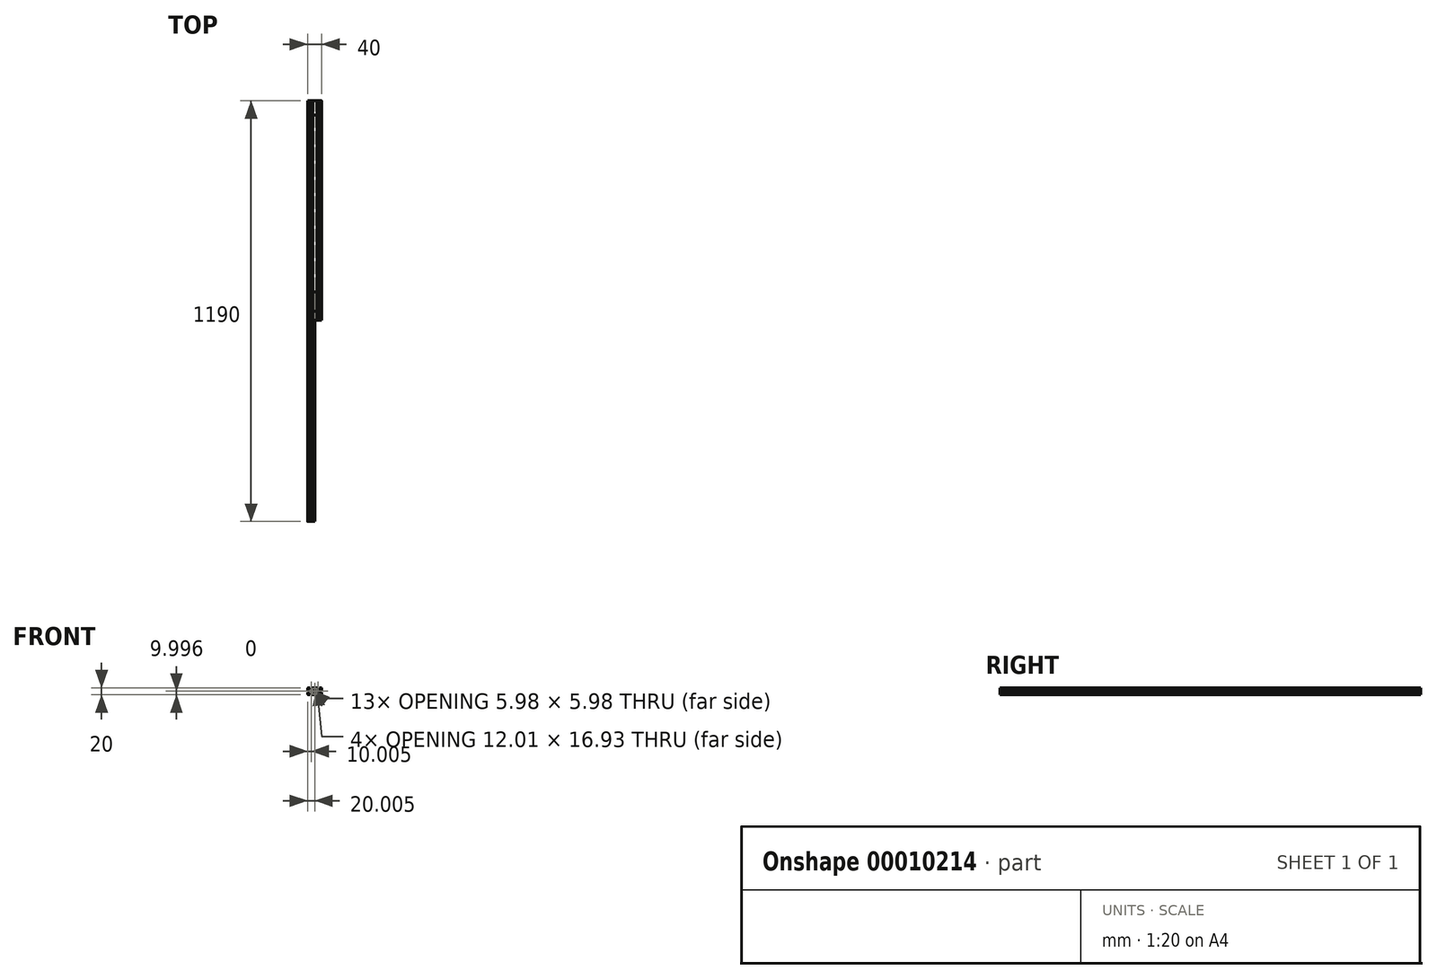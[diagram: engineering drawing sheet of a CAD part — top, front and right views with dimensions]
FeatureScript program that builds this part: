
annotation { "Feature Type Name" : "Feature", "Feature Type Description" : "" }
export const myFeature = defineFeature(function(context is Context, id is Id, definition is map)
    precondition{}
    {
        {
            var Q0;
            Q0=qCreatedBy(makeId("Front.planeOp"),FACE);
            var sketch = newSketch(context, id + "F0", { "sketchPlane" : qUnion([Q0])});
            skLineSegment(sketch, "E0.rect.bottom", {"start": v(-8.26, 10.09) * mm, "end": v(-3.52, 10.09) * mm});
            skLineSegment(sketch, "E0.rect.top", {"start": v(-8.26, -9.91) * mm, "end": v(-3.52, -9.91) * mm});
            skLineSegment(sketch, "E0.rect.left", {"start": v(-10, 8.34) * mm, "end": v(-10, 3.6) * mm});
            skLineSegment(sketch, "E0.rect.right", {"start": v(10, 8.34) * mm, "end": v(10, 3.6) * mm});
            skPoint(sketch, "E0.rect.middle", {"position": v(0, 0.09) * mm});
            skPoint(sketch, "E1.visualSharp", {"position": v(-10, 10.09) * mm});
            skArc(sketch, "E1.filletArc", {"start": v(-8.26, 10.09) * mm, "mid": v(-9.5, 9.57) * mm, "end": v(-10, 8.34) * mm});
            skPoint(sketch, "E2.visualSharp", {"position": v(10, 10.09) * mm});
            skArc(sketch, "E2.filletArc", {"start": v(10, 8.34) * mm, "mid": v(9.48, 9.57) * mm, "end": v(8.24, 10.09) * mm});
            skPoint(sketch, "E3.visualSharp", {"position": v(10, -9.91) * mm});
            skArc(sketch, "E3.filletArc", {"start": v(8.24, -9.91) * mm, "mid": v(9.48, -9.4) * mm, "end": v(10, -8.16) * mm});
            skPoint(sketch, "E4.visualSharp", {"position": v(-10, -9.91) * mm});
            skArc(sketch, "E4.filletArc", {"start": v(-10, -8.16) * mm, "mid": v(-9.5, -9.4) * mm, "end": v(-8.26, -9.91) * mm});
            skPoint(sketch, "E5.rect.middle", {"position": v(-10, 0.09) * mm});
            skPoint(sketch, "E6.rect.middle", {"position": v(0, -9.91) * mm});
            skPoint(sketch, "E7.4.MirrorP", {"position": v(0, 10.09) * mm});
            skPoint(sketch, "E8.4.MirrorP", {"position": v(10, 0.09) * mm});
            skLineSegment(sketch, "E9", {"start": v(-3, 9.47) * mm, "end": v(-3, 8.55) * mm});
            skLineSegment(sketch, "E10", {"start": v(-3, 8.55) * mm, "end": v(-6.2, 8.55) * mm});
            skLineSegment(sketch, "E11", {"start": v(-6.2, 8.55) * mm, "end": v(-6.2, 6.99) * mm});
            skLineSegment(sketch, "E12", {"start": v(-0.58, 4.59) * mm, "end": v(-3.8, 4.59) * mm});
            skLineSegment(sketch, "E13", {"start": v(-3.8, 4.59) * mm, "end": v(-6.2, 6.99) * mm});
            skLineSegment(sketch, "E14", {"start": v(-3.52, 10.09) * mm, "end": v(-3.52, 9.47) * mm});
            skLineSegment(sketch, "E15", {"start": v(-3.52, 9.47) * mm, "end": v(-3, 9.47) * mm});
            skLineSegment(sketch, "E16", {"start": v(0, 28.9) * mm, "end": v(0, 4.59) * mm});
            skLineSegment(sketch, "E17.0.MirrorCS", {"start": v(3.51, 10.09) * mm, "end": v(3.51, 9.47) * mm});
            skLineSegment(sketch, "E18.0.MirrorCS", {"start": v(3.51, 9.47) * mm, "end": v(3, 9.47) * mm});
            skLineSegment(sketch, "E19.0.MirrorCS", {"start": v(3, 8.55) * mm, "end": v(6.2, 8.55) * mm});
            skLineSegment(sketch, "E20.0.MirrorCS", {"start": v(6.2, 8.55) * mm, "end": v(6.2, 6.99) * mm});
            skLineSegment(sketch, "E21.0.MirrorCS", {"start": v(3.8, 4.59) * mm, "end": v(6.2, 6.99) * mm});
            skLineSegment(sketch, "E22.0.MirrorCS", {"start": v(3.51, -9.91) * mm, "end": v(3.51, -9.3) * mm});
            skLineSegment(sketch, "E23.0.MirrorCS", {"start": v(3.51, -9.3) * mm, "end": v(3, -9.3) * mm});
            skLineSegment(sketch, "E24.0.MirrorCS", {"start": v(3, -8.38) * mm, "end": v(6.2, -8.38) * mm});
            skLineSegment(sketch, "E25.0.MirrorCS", {"start": v(6.2, -8.38) * mm, "end": v(6.2, -6.81) * mm});
            skLineSegment(sketch, "E26.0.MirrorCS", {"start": v(3.8, -4.41) * mm, "end": v(6.2, -6.81) * mm});
            skLineSegment(sketch, "E27.0.MirrorCS", {"start": v(-0.58, -4.41) * mm, "end": v(-3.8, -4.41) * mm});
            skLineSegment(sketch, "E28.0.MirrorCS", {"start": v(-3.8, -4.41) * mm, "end": v(-6.2, -6.81) * mm});
            skLineSegment(sketch, "E29.0.MirrorCS", {"start": v(-6.2, -8.38) * mm, "end": v(-6.2, -6.81) * mm});
            skLineSegment(sketch, "E30.0.MirrorCS", {"start": v(-3, -8.38) * mm, "end": v(-6.2, -8.38) * mm});
            skLineSegment(sketch, "E31.0.MirrorCS", {"start": v(-3.52, -9.3) * mm, "end": v(-3, -9.3) * mm});
            skLineSegment(sketch, "E32.0.MirrorCS", {"start": v(-3.52, -9.91) * mm, "end": v(-3.52, -9.3) * mm});
            skLineSegment(sketch, "E33.0.MirrorCS", {"start": v(10, 3.6) * mm, "end": v(9.38, 3.6) * mm});
            skLineSegment(sketch, "E34.0.MirrorCS", {"start": v(9.38, 3.6) * mm, "end": v(9.38, 3.09) * mm});
            skLineSegment(sketch, "E35.0.MirrorCS", {"start": v(8.46, 3.09) * mm, "end": v(8.46, 6.29) * mm});
            skLineSegment(sketch, "E36.0.MirrorCS", {"start": v(8.46, 6.29) * mm, "end": v(6.9, 6.29) * mm});
            skLineSegment(sketch, "E37.0.MirrorCS", {"start": v(4.5, 3.89) * mm, "end": v(6.9, 6.29) * mm});
            skLineSegment(sketch, "E38.0.MirrorCS", {"start": v(4.5, 0.56) * mm, "end": v(4.5, 3.89) * mm});
            skLineSegment(sketch, "E39.0.MirrorCS", {"start": v(4.5, -3.71) * mm, "end": v(6.9, -6.11) * mm});
            skLineSegment(sketch, "E40.0.MirrorCS", {"start": v(8.46, -6.11) * mm, "end": v(6.9, -6.11) * mm});
            skLineSegment(sketch, "E41.0.MirrorCS", {"start": v(8.46, -2.91) * mm, "end": v(8.46, -6.11) * mm});
            skLineSegment(sketch, "E42.0.MirrorCS", {"start": v(9.38, -3.43) * mm, "end": v(9.38, -2.91) * mm});
            skLineSegment(sketch, "E43.0.MirrorCS", {"start": v(10, -3.43) * mm, "end": v(9.38, -3.43) * mm});
            skLineSegment(sketch, "E44.0.MirrorCS", {"start": v(-4.5, -3.71) * mm, "end": v(-6.9, -6.11) * mm});
            skLineSegment(sketch, "E45.0.MirrorCS", {"start": v(-8.47, -6.11) * mm, "end": v(-6.9, -6.11) * mm});
            skLineSegment(sketch, "E46.0.MirrorCS", {"start": v(-8.47, -2.91) * mm, "end": v(-8.47, -6.11) * mm});
            skLineSegment(sketch, "E47.0.MirrorCS", {"start": v(-4.5, 3.89) * mm, "end": v(-6.9, 6.29) * mm});
            skLineSegment(sketch, "E48.0.MirrorCS", {"start": v(-8.47, 6.29) * mm, "end": v(-6.9, 6.29) * mm});
            skLineSegment(sketch, "E49.0.MirrorCS", {"start": v(-8.47, 3.09) * mm, "end": v(-8.47, 6.29) * mm});
            skLineSegment(sketch, "E50.0.MirrorCS", {"start": v(-9.39, 3.6) * mm, "end": v(-9.39, 3.09) * mm});
            skLineSegment(sketch, "E51.0.MirrorCS", {"start": v(-10, 3.6) * mm, "end": v(-9.39, 3.6) * mm});
            skLineSegment(sketch, "E52.0.MirrorCS", {"start": v(-9.39, -3.43) * mm, "end": v(-9.39, -2.91) * mm});
            skLineSegment(sketch, "E53.0.MirrorCS", {"start": v(-10, -3.43) * mm, "end": v(-9.39, -3.43) * mm});
            skPoint(sketch, "E54", {"position": v(3, 10.09) * mm});
            skPoint(sketch, "E55", {"position": v(-3, 9.47) * mm});
            skPoint(sketch, "E56", {"position": v(-3, 10.09) * mm});
            skPoint(sketch, "E57", {"position": v(3, 9.47) * mm});
            skPoint(sketch, "E58", {"position": v(3.51, 10.09) * mm});
            skPoint(sketch, "E59", {"position": v(-3, 8.55) * mm});
            skPoint(sketch, "E60", {"position": v(-6.2, 8.55) * mm});
            skPoint(sketch, "E61", {"position": v(-6.2, 6.99) * mm});
            skPoint(sketch, "E62", {"position": v(-3.8, 4.59) * mm});
            skPoint(sketch, "E63", {"position": v(3.8, 4.59) * mm});
            skPoint(sketch, "E64", {"position": v(6.2, 6.99) * mm});
            skPoint(sketch, "E65", {"position": v(6.2, 8.55) * mm});
            skPoint(sketch, "E66", {"position": v(3, 8.55) * mm});
            skLineSegment(sketch, "E67.trimOffspring", {"start": v(3, 9.47) * mm, "end": v(3, 8.55) * mm});
            skLineSegment(sketch, "E68.trimOffspring", {"start": v(3.51, 10.09) * mm, "end": v(8.24, 10.09) * mm});
            skPoint(sketch, "E69.orphan", {"position": v(-3, 15.59) * mm});
            skPoint(sketch, "E7.2.MirrorCS.end.orphan", {"position": v(3, 15.59) * mm});
            skPoint(sketch, "E70", {"position": v(-10, 3.6) * mm});
            skPoint(sketch, "E71", {"position": v(-10, 3.09) * mm});
            skPoint(sketch, "E72", {"position": v(-9.39, 3.6) * mm});
            skPoint(sketch, "E73", {"position": v(-9.39, 3.09) * mm});
            skPoint(sketch, "E74", {"position": v(-8.47, 3.09) * mm});
            skPoint(sketch, "E75", {"position": v(-8.47, 6.29) * mm});
            skPoint(sketch, "E76", {"position": v(-6.9, 6.29) * mm});
            skPoint(sketch, "E77", {"position": v(-4.5, 3.89) * mm});
            skPoint(sketch, "E78", {"position": v(-4.5, -3.71) * mm});
            skPoint(sketch, "E79", {"position": v(-6.9, -6.11) * mm});
            skPoint(sketch, "E80", {"position": v(-8.44, -6.12) * mm});
            skPoint(sketch, "E81", {"position": v(-8.47, -2.91) * mm});
            skPoint(sketch, "E82", {"position": v(-9.39, -2.91) * mm});
            skPoint(sketch, "E83", {"position": v(-9.39, -3.43) * mm});
            skPoint(sketch, "E84", {"position": v(-10, -3.43) * mm});
            skPoint(sketch, "E85", {"position": v(-10, -2.91) * mm});
            skPoint(sketch, "E86", {"position": v(-3.52, -9.91) * mm});
            skPoint(sketch, "E87", {"position": v(-3, -9.91) * mm});
            skPoint(sketch, "E88", {"position": v(-3, -9.3) * mm});
            skPoint(sketch, "E89", {"position": v(-3.52, -9.3) * mm});
            skPoint(sketch, "E90", {"position": v(-3, -8.38) * mm});
            skPoint(sketch, "E91", {"position": v(-6.2, -8.38) * mm});
            skPoint(sketch, "E92", {"position": v(-6.2, -6.81) * mm});
            skPoint(sketch, "E93", {"position": v(-3.8, -4.41) * mm});
            skPoint(sketch, "E94", {"position": v(3.8, -4.41) * mm});
            skPoint(sketch, "E95", {"position": v(6.2, -6.81) * mm});
            skPoint(sketch, "E96", {"position": v(6.2, -8.38) * mm});
            skPoint(sketch, "E97", {"position": v(3, -8.38) * mm});
            skPoint(sketch, "E98", {"position": v(3, -9.3) * mm});
            skPoint(sketch, "E99", {"position": v(3.51, -9.3) * mm});
            skPoint(sketch, "E100", {"position": v(3, -9.91) * mm});
            skPoint(sketch, "E101", {"position": v(3.51, -9.91) * mm});
            skPoint(sketch, "E102", {"position": v(10, -3.43) * mm});
            skPoint(sketch, "E103", {"position": v(10, -2.91) * mm});
            skPoint(sketch, "E104", {"position": v(9.38, -2.91) * mm});
            skPoint(sketch, "E105", {"position": v(9.38, -3.43) * mm});
            skPoint(sketch, "E106", {"position": v(8.46, -2.91) * mm});
            skPoint(sketch, "E107", {"position": v(8.46, -6.11) * mm});
            skPoint(sketch, "E108", {"position": v(6.9, -6.11) * mm});
            skPoint(sketch, "E109", {"position": v(4.5, -3.71) * mm});
            skPoint(sketch, "E110", {"position": v(4.5, 3.89) * mm});
            skPoint(sketch, "E111", {"position": v(6.9, 6.29) * mm});
            skPoint(sketch, "E112", {"position": v(8.46, 6.29) * mm});
            skPoint(sketch, "E113", {"position": v(8.46, 3.09) * mm});
            skPoint(sketch, "E114", {"position": v(9.38, 3.09) * mm});
            skPoint(sketch, "E115", {"position": v(9.38, 3.6) * mm});
            skPoint(sketch, "E116", {"position": v(10, 3.6) * mm});
            skPoint(sketch, "E117", {"position": v(10, 3.09) * mm});
            skLineSegment(sketch, "E118.trimOffspring", {"start": v(10, -3.43) * mm, "end": v(10, -8.16) * mm});
            skLineSegment(sketch, "E119.trimOffspring", {"start": v(9.38, 3.09) * mm, "end": v(8.46, 3.09) * mm});
            skPoint(sketch, "E8.1.MirrorCS.start.orphan", {"position": v(15.5, 3.09) * mm});
            skLineSegment(sketch, "E120.trimOffspring", {"start": v(9.38, -2.91) * mm, "end": v(8.46, -2.91) * mm});
            skPoint(sketch, "E8.2.MirrorCS.start.orphan", {"position": v(15.5, -2.91) * mm});
            skLineSegment(sketch, "E121.trimOffspring", {"start": v(3.51, -9.91) * mm, "end": v(8.24, -9.91) * mm});
            skLineSegment(sketch, "E122.trimOffspring", {"start": v(3, -9.3) * mm, "end": v(3, -8.38) * mm});
            skLineSegment(sketch, "E123.trimOffspring", {"start": v(-3, -9.3) * mm, "end": v(-3, -8.38) * mm});
            skPoint(sketch, "E124.orphan", {"position": v(3, -15.41) * mm});
            skPoint(sketch, "E6.rect.bottom.start.orphan", {"position": v(-3, -15.41) * mm});
            skLineSegment(sketch, "E125.trimOffspring", {"start": v(-10, -3.43) * mm, "end": v(-10, -8.16) * mm});
            skLineSegment(sketch, "E126.trimOffspring", {"start": v(-9.39, -2.91) * mm, "end": v(-8.47, -2.91) * mm});
            skLineSegment(sketch, "E127.trimOffspring", {"start": v(-9.39, 3.09) * mm, "end": v(-8.47, 3.09) * mm});
            skPoint(sketch, "E5.rect.left.end.orphan", {"position": v(-15.5, -2.91) * mm});
            skPoint(sketch, "E5.rect.left.start.orphan", {"position": v(-15.5, 3.09) * mm});
            skArc(sketch, "E128", {"start": v(1.01, 2.64) * mm, "mid": v(0, 2.84) * mm, "end": v(-1.02, 2.64) * mm});
            skLineSegment(sketch, "E129", {"start": v(-0.58, 4.59) * mm, "end": v(0, 4.02) * mm});
            skLineSegment(sketch, "E130", {"start": v(-4.5, 0.56) * mm, "end": v(-4, 0.09) * mm});
            skLineSegment(sketch, "E131.0.MirrorCS", {"start": v(0.57, 4.59) * mm, "end": v(0, 4.02) * mm});
            skLineSegment(sketch, "E132.0.MirrorCS", {"start": v(4.5, 0.56) * mm, "end": v(4, 0.09) * mm});
            skLineSegment(sketch, "E133.0.MirrorCS", {"start": v(-4.5, -0.4) * mm, "end": v(-4, 0.09) * mm});
            skLineSegment(sketch, "E134.0.MirrorCS", {"start": v(4.5, -0.4) * mm, "end": v(4, 0.09) * mm});
            skLineSegment(sketch, "E135.0.MirrorCS", {"start": v(0.57, -4.41) * mm, "end": v(0, -3.84) * mm});
            skLineSegment(sketch, "E136.0.MirrorCS", {"start": v(-0.58, -4.41) * mm, "end": v(0, -3.84) * mm});
            skPoint(sketch, "E137.orphan", {"position": v(0, -4.41) * mm});
            skLineSegment(sketch, "E138", {"start": v(8.24, -8.16) * mm, "end": v(-10.9, 10.99) * mm, "construction": true});
            skLineSegment(sketch, "E139", {"start": v(-5.8, -1.82) * mm, "end": v(1.97, 5.95) * mm, "construction": true});
            skLineSegment(sketch, "E140", {"start": v(-3, 1.54) * mm, "end": v(-2.56, 1.1) * mm});
            skLineSegment(sketch, "E141.0.MirrorCS", {"start": v(-1.46, 3.08) * mm, "end": v(-1.02, 2.64) * mm});
            skLineSegment(sketch, "E142.0.MirrorCS", {"start": v(1.45, 3.08) * mm, "end": v(1.01, 2.64) * mm});
            skLineSegment(sketch, "E143.0.MirrorCS", {"start": v(2.98, 1.54) * mm, "end": v(2.55, 1.1) * mm});
            skLineSegment(sketch, "E144.0.MirrorCS", {"start": v(2.98, -1.37) * mm, "end": v(2.55, -0.93) * mm});
            skLineSegment(sketch, "E145.0.MirrorCS", {"start": v(1.45, -2.9) * mm, "end": v(1.01, -2.47) * mm});
            skLineSegment(sketch, "E146.0.MirrorCS", {"start": v(-1.46, -2.9) * mm, "end": v(-1.02, -2.47) * mm});
            skLineSegment(sketch, "E147.0.MirrorCS", {"start": v(-3, -1.37) * mm, "end": v(-2.56, -0.93) * mm});
            skArc(sketch, "E148.trimOffspring", {"start": v(-1.02, -2.47) * mm, "mid": v(0, -2.66) * mm, "end": v(1.01, -2.47) * mm});
            skArc(sketch, "E149.trimOffspring", {"start": v(2.55, -0.93) * mm, "mid": v(2.74, 0.09) * mm, "end": v(2.55, 1.1) * mm});
            skArc(sketch, "E150.trimOffspring", {"start": v(-2.56, 1.1) * mm, "mid": v(-2.76, 0.09) * mm, "end": v(-2.56, -0.93) * mm});
            skLineSegment(sketch, "E151", {"start": v(-3, -1.37) * mm, "end": v(-1.46, -2.9) * mm});
            skLineSegment(sketch, "E152", {"start": v(1.45, 3.08) * mm, "end": v(2.98, 1.54) * mm});
            skLineSegment(sketch, "E153", {"start": v(-1.46, 3.08) * mm, "end": v(-3, 1.54) * mm});
            skLineSegment(sketch, "E154", {"start": v(2.98, -1.37) * mm, "end": v(1.45, -2.9) * mm});
            skLineSegment(sketch, "E155", {"start": v(-4.5, 3.89) * mm, "end": v(-4.5, 0.56) * mm});
            skLineSegment(sketch, "E156", {"start": v(-4.5, -0.4) * mm, "end": v(-4.5, -3.71) * mm});
            skLineSegment(sketch, "E157", {"start": v(4.5, -0.4) * mm, "end": v(4.5, -3.71) * mm});
            skLineSegment(sketch, "E158", {"start": v(0.57, 4.59) * mm, "end": v(3.8, 4.59) * mm});
            skLineSegment(sketch, "E159", {"start": v(0.57, -4.41) * mm, "end": v(3.8, -4.41) * mm});
            skSolve(sketch);
        }
        {
            var Q0;
            Q0=qCreatedBy(makeId("Front.planeOp"),FACE);
            var sketch = newSketch(context, id + "F1", { "sketchPlane" : qUnion([Q0])});
            skLineSegment(sketch, "E160.0.0", {"start": v(-3.52, 10.09) * mm, "end": v(-8.26, 10.09) * mm});
            skArc(sketch, "E160.0.1", {"start": v(-8.26, 10.09) * mm, "mid": v(-9.5, 9.57) * mm, "end": v(-10, 8.34) * mm});
            skLineSegment(sketch, "E160.0.2", {"start": v(-10, 8.34) * mm, "end": v(-10, 3.6) * mm});
            skLineSegment(sketch, "E160.0.3", {"start": v(-10, 3.6) * mm, "end": v(-9.39, 3.6) * mm});
            skLineSegment(sketch, "E160.0.4", {"start": v(-9.39, 3.6) * mm, "end": v(-9.39, 3.09) * mm});
            skLineSegment(sketch, "E160.0.5", {"start": v(-9.39, 3.09) * mm, "end": v(-8.47, 3.09) * mm});
            skLineSegment(sketch, "E160.0.6", {"start": v(-8.47, 3.09) * mm, "end": v(-8.47, 6.29) * mm});
            skLineSegment(sketch, "E160.0.7", {"start": v(-8.47, 6.29) * mm, "end": v(-6.9, 6.29) * mm});
            skLineSegment(sketch, "E160.0.8", {"start": v(-6.9, 6.29) * mm, "end": v(-4.5, 3.89) * mm});
            skLineSegment(sketch, "E160.0.9", {"start": v(-4.5, 3.89) * mm, "end": v(-4.5, 0.56) * mm});
            skLineSegment(sketch, "E160.0.10", {"start": v(-4.5, 0.56) * mm, "end": v(-4, 0.09) * mm});
            skLineSegment(sketch, "E160.0.11", {"start": v(-4, 0.09) * mm, "end": v(-4.5, -0.4) * mm});
            skLineSegment(sketch, "E160.0.12", {"start": v(-4.5, -0.4) * mm, "end": v(-4.5, -3.71) * mm});
            skLineSegment(sketch, "E160.0.13", {"start": v(-4.5, -3.71) * mm, "end": v(-6.9, -6.11) * mm});
            skLineSegment(sketch, "E160.0.14", {"start": v(-6.9, -6.11) * mm, "end": v(-8.47, -6.11) * mm});
            skLineSegment(sketch, "E160.0.15", {"start": v(-8.47, -6.11) * mm, "end": v(-8.47, -2.91) * mm});
            skLineSegment(sketch, "E160.0.16", {"start": v(-8.47, -2.91) * mm, "end": v(-9.39, -2.91) * mm});
            skLineSegment(sketch, "E160.0.17", {"start": v(-9.39, -2.91) * mm, "end": v(-9.39, -3.43) * mm});
            skLineSegment(sketch, "E160.0.18", {"start": v(-9.39, -3.43) * mm, "end": v(-10, -3.43) * mm});
            skLineSegment(sketch, "E160.0.19", {"start": v(-10, -3.43) * mm, "end": v(-10, -8.16) * mm});
            skArc(sketch, "E160.0.20", {"start": v(-10, -8.16) * mm, "mid": v(-9.5, -9.4) * mm, "end": v(-8.26, -9.91) * mm});
            skLineSegment(sketch, "E160.0.21", {"start": v(-8.26, -9.91) * mm, "end": v(-3.52, -9.91) * mm});
            skLineSegment(sketch, "E160.0.22", {"start": v(-3.52, -9.91) * mm, "end": v(-3.52, -9.3) * mm});
            skLineSegment(sketch, "E160.0.23", {"start": v(-3.52, -9.3) * mm, "end": v(-3, -9.3) * mm});
            skLineSegment(sketch, "E160.0.24", {"start": v(-3, -9.3) * mm, "end": v(-3, -8.38) * mm});
            skLineSegment(sketch, "E160.0.25", {"start": v(-3, -8.38) * mm, "end": v(-6.2, -8.38) * mm});
            skLineSegment(sketch, "E160.0.26", {"start": v(-6.2, -8.38) * mm, "end": v(-6.2, -6.81) * mm});
            skLineSegment(sketch, "E160.0.27", {"start": v(-6.2, -6.81) * mm, "end": v(-3.8, -4.41) * mm});
            skLineSegment(sketch, "E160.0.28", {"start": v(-3.8, -4.41) * mm, "end": v(-0.58, -4.41) * mm});
            skLineSegment(sketch, "E160.0.29", {"start": v(-0.58, -4.41) * mm, "end": v(0, -3.84) * mm});
            skLineSegment(sketch, "E160.0.30", {"start": v(0, -3.84) * mm, "end": v(0.57, -4.41) * mm});
            skLineSegment(sketch, "E160.0.31", {"start": v(0.57, -4.41) * mm, "end": v(3.8, -4.41) * mm});
            skLineSegment(sketch, "E160.0.32", {"start": v(3.8, -4.41) * mm, "end": v(6.2, -6.81) * mm});
            skLineSegment(sketch, "E160.0.33", {"start": v(6.2, -6.81) * mm, "end": v(6.2, -8.38) * mm});
            skLineSegment(sketch, "E160.0.34", {"start": v(6.2, -8.38) * mm, "end": v(3, -8.38) * mm});
            skLineSegment(sketch, "E160.0.35", {"start": v(3, -8.38) * mm, "end": v(3, -9.3) * mm});
            skLineSegment(sketch, "E160.0.36", {"start": v(3, -9.3) * mm, "end": v(3.51, -9.3) * mm});
            skLineSegment(sketch, "E160.0.37", {"start": v(3.51, -9.3) * mm, "end": v(3.51, -9.91) * mm});
            skLineSegment(sketch, "E160.0.47", {"start": v(4.5, -3.71) * mm, "end": v(4.5, -0.4) * mm});
            skLineSegment(sketch, "E160.0.48", {"start": v(4.5, -0.4) * mm, "end": v(4, 0.09) * mm});
            skLineSegment(sketch, "E160.0.49", {"start": v(4, 0.09) * mm, "end": v(4.5, 0.56) * mm});
            skLineSegment(sketch, "E160.0.50", {"start": v(4.5, 0.56) * mm, "end": v(4.5, 3.89) * mm});
            skLineSegment(sketch, "E160.0.60", {"start": v(3.51, 10.09) * mm, "end": v(3.51, 9.47) * mm});
            skLineSegment(sketch, "E160.0.61", {"start": v(3.51, 9.47) * mm, "end": v(3, 9.47) * mm});
            skLineSegment(sketch, "E160.0.62", {"start": v(3, 9.47) * mm, "end": v(3, 8.55) * mm});
            skLineSegment(sketch, "E160.0.63", {"start": v(3, 8.55) * mm, "end": v(6.2, 8.55) * mm});
            skLineSegment(sketch, "E160.0.64", {"start": v(6.2, 8.55) * mm, "end": v(6.2, 6.99) * mm});
            skLineSegment(sketch, "E160.0.65", {"start": v(6.2, 6.99) * mm, "end": v(3.8, 4.59) * mm});
            skLineSegment(sketch, "E160.0.66", {"start": v(3.8, 4.59) * mm, "end": v(0.57, 4.59) * mm});
            skLineSegment(sketch, "E160.0.67", {"start": v(0.57, 4.59) * mm, "end": v(0, 4.02) * mm});
            skLineSegment(sketch, "E160.0.68", {"start": v(0, 4.02) * mm, "end": v(-0.58, 4.59) * mm});
            skLineSegment(sketch, "E160.0.69", {"start": v(-0.58, 4.59) * mm, "end": v(-3.8, 4.59) * mm});
            skLineSegment(sketch, "E160.0.70", {"start": v(-3.8, 4.59) * mm, "end": v(-6.2, 6.99) * mm});
            skLineSegment(sketch, "E160.0.71", {"start": v(-6.2, 6.99) * mm, "end": v(-6.2, 8.55) * mm});
            skLineSegment(sketch, "E160.0.72", {"start": v(-6.2, 8.55) * mm, "end": v(-3, 8.55) * mm});
            skLineSegment(sketch, "E160.0.73", {"start": v(-3, 8.55) * mm, "end": v(-3, 9.47) * mm});
            skLineSegment(sketch, "E160.0.74", {"start": v(-3, 9.47) * mm, "end": v(-3.52, 9.47) * mm});
            skLineSegment(sketch, "E160.0.75", {"start": v(-3.52, 9.47) * mm, "end": v(-3.52, 10.09) * mm});
            skLineSegment(sketch, "E161.0.0", {"start": v(1.45, 3.08) * mm, "end": v(1.01, 2.64) * mm});
            skArc(sketch, "E161.0.1", {"start": v(1.01, 2.64) * mm, "mid": v(0, 2.84) * mm, "end": v(-1.02, 2.64) * mm});
            skLineSegment(sketch, "E161.0.2", {"start": v(-1.02, 2.64) * mm, "end": v(-1.46, 3.08) * mm});
            skLineSegment(sketch, "E161.0.3", {"start": v(-1.46, 3.08) * mm, "end": v(-3, 1.54) * mm});
            skLineSegment(sketch, "E161.0.4", {"start": v(-3, 1.54) * mm, "end": v(-2.56, 1.1) * mm});
            skArc(sketch, "E161.0.5", {"start": v(-2.56, 1.1) * mm, "mid": v(-2.76, 0.09) * mm, "end": v(-2.56, -0.93) * mm});
            skLineSegment(sketch, "E161.0.6", {"start": v(-2.56, -0.93) * mm, "end": v(-3, -1.37) * mm});
            skLineSegment(sketch, "E161.0.7", {"start": v(-3, -1.37) * mm, "end": v(-1.46, -2.9) * mm});
            skLineSegment(sketch, "E161.0.8", {"start": v(-1.46, -2.9) * mm, "end": v(-1.02, -2.47) * mm});
            skArc(sketch, "E161.0.9", {"start": v(-1.02, -2.47) * mm, "mid": v(0, -2.66) * mm, "end": v(1.01, -2.47) * mm});
            skLineSegment(sketch, "E161.0.10", {"start": v(1.01, -2.47) * mm, "end": v(1.45, -2.9) * mm});
            skLineSegment(sketch, "E161.0.11", {"start": v(1.45, -2.9) * mm, "end": v(2.98, -1.37) * mm});
            skLineSegment(sketch, "E161.0.12", {"start": v(2.98, -1.37) * mm, "end": v(2.55, -0.93) * mm});
            skArc(sketch, "E161.0.13", {"start": v(2.55, -0.93) * mm, "mid": v(2.74, 0.09) * mm, "end": v(2.55, 1.1) * mm});
            skLineSegment(sketch, "E161.0.14", {"start": v(2.55, 1.1) * mm, "end": v(2.98, 1.54) * mm});
            skLineSegment(sketch, "E161.0.15", {"start": v(2.98, 1.54) * mm, "end": v(1.45, 3.08) * mm});
            skLineSegment(sketch, "E162", {"start": v(10, 11.4) * mm, "end": v(10, -11.43) * mm, "construction": true});
            skLineSegment(sketch, "E163.0.MirrorCS", {"start": v(16.48, 10.09) * mm, "end": v(16.48, 9.47) * mm});
            skLineSegment(sketch, "E164.0.MirrorCS", {"start": v(16.48, 9.47) * mm, "end": v(17, 9.47) * mm});
            skLineSegment(sketch, "E165.0.MirrorCS", {"start": v(17, 9.47) * mm, "end": v(17, 8.55) * mm});
            skLineSegment(sketch, "E166.0.MirrorCS", {"start": v(17, 8.55) * mm, "end": v(13.8, 8.55) * mm});
            skLineSegment(sketch, "E167.0.MirrorCS", {"start": v(13.8, 8.55) * mm, "end": v(13.8, 6.99) * mm});
            skLineSegment(sketch, "E168.0.MirrorCS", {"start": v(13.8, 6.99) * mm, "end": v(16.2, 4.59) * mm});
            skLineSegment(sketch, "E169.0.MirrorCS", {"start": v(16.2, 4.59) * mm, "end": v(19.42, 4.59) * mm});
            skLineSegment(sketch, "E170.0.MirrorCS", {"start": v(19.42, 4.59) * mm, "end": v(20, 4.02) * mm});
            skLineSegment(sketch, "E171.0.MirrorCS", {"start": v(20, 4.02) * mm, "end": v(20.57, 4.59) * mm});
            skLineSegment(sketch, "E172.0.MirrorCS", {"start": v(20.57, 4.59) * mm, "end": v(23.8, 4.59) * mm});
            skLineSegment(sketch, "E173.0.MirrorCS", {"start": v(23.8, 4.59) * mm, "end": v(26.2, 6.99) * mm});
            skLineSegment(sketch, "E174.0.MirrorCS", {"start": v(26.2, 6.99) * mm, "end": v(26.2, 8.55) * mm});
            skLineSegment(sketch, "E175.0.MirrorCS", {"start": v(26.2, 8.55) * mm, "end": v(23, 8.55) * mm});
            skLineSegment(sketch, "E176.0.MirrorCS", {"start": v(23, 8.55) * mm, "end": v(23, 9.47) * mm});
            skLineSegment(sketch, "E177.0.MirrorCS", {"start": v(23, 9.47) * mm, "end": v(23.51, 9.47) * mm});
            skLineSegment(sketch, "E178.0.MirrorCS", {"start": v(23.51, 9.47) * mm, "end": v(23.51, 10.09) * mm});
            skLineSegment(sketch, "E179.0.MirrorCS", {"start": v(23.51, 10.09) * mm, "end": v(28.24, 10.09) * mm});
            skArc(sketch, "E180.0.MirrorCS", {"start": v(28.24, 10.09) * mm, "mid": v(29.48, 9.57) * mm, "end": v(30, 8.34) * mm});
            skLineSegment(sketch, "E181.0.MirrorCS", {"start": v(30, 8.34) * mm, "end": v(30, 3.6) * mm});
            skLineSegment(sketch, "E182.0.MirrorCS", {"start": v(30, 3.6) * mm, "end": v(29.38, 3.6) * mm});
            skLineSegment(sketch, "E183.0.MirrorCS", {"start": v(29.38, 3.6) * mm, "end": v(29.38, 3.09) * mm});
            skLineSegment(sketch, "E184.0.MirrorCS", {"start": v(29.38, 3.09) * mm, "end": v(28.46, 3.09) * mm});
            skLineSegment(sketch, "E185.0.MirrorCS", {"start": v(28.46, 3.09) * mm, "end": v(28.46, 6.29) * mm});
            skLineSegment(sketch, "E186.0.MirrorCS", {"start": v(28.46, 6.29) * mm, "end": v(26.9, 6.29) * mm});
            skLineSegment(sketch, "E187.0.MirrorCS", {"start": v(26.9, 6.29) * mm, "end": v(24.5, 3.89) * mm});
            skLineSegment(sketch, "E188.0.MirrorCS", {"start": v(24.5, 3.89) * mm, "end": v(24.5, 0.56) * mm});
            skLineSegment(sketch, "E189.0.MirrorCS", {"start": v(24.5, 0.56) * mm, "end": v(24, 0.09) * mm});
            skLineSegment(sketch, "E190.0.MirrorCS", {"start": v(24, 0.09) * mm, "end": v(24.5, -0.4) * mm});
            skLineSegment(sketch, "E191.0.MirrorCS", {"start": v(24.5, -0.4) * mm, "end": v(24.5, -3.71) * mm});
            skLineSegment(sketch, "E192.0.MirrorCS", {"start": v(24.5, -3.71) * mm, "end": v(26.9, -6.11) * mm});
            skLineSegment(sketch, "E193.0.MirrorCS", {"start": v(26.9, -6.11) * mm, "end": v(28.46, -6.11) * mm});
            skLineSegment(sketch, "E194.0.MirrorCS", {"start": v(28.46, -6.11) * mm, "end": v(28.46, -2.91) * mm});
            skLineSegment(sketch, "E195.0.MirrorCS", {"start": v(28.46, -2.91) * mm, "end": v(29.38, -2.91) * mm});
            skLineSegment(sketch, "E196.0.MirrorCS", {"start": v(29.38, -2.91) * mm, "end": v(29.38, -3.43) * mm});
            skLineSegment(sketch, "E197.0.MirrorCS", {"start": v(29.38, -3.43) * mm, "end": v(30, -3.43) * mm});
            skLineSegment(sketch, "E198.0.MirrorCS", {"start": v(30, -3.43) * mm, "end": v(30, -8.16) * mm});
            skArc(sketch, "E199.0.MirrorCS", {"start": v(30, -8.16) * mm, "mid": v(29.48, -9.4) * mm, "end": v(28.24, -9.91) * mm});
            skLineSegment(sketch, "E200.0.MirrorCS", {"start": v(28.24, -9.91) * mm, "end": v(23.51, -9.91) * mm});
            skLineSegment(sketch, "E201.0.MirrorCS", {"start": v(23.51, -9.91) * mm, "end": v(23.51, -9.3) * mm});
            skLineSegment(sketch, "E202.0.MirrorCS", {"start": v(23.51, -9.3) * mm, "end": v(23, -9.3) * mm});
            skLineSegment(sketch, "E203.0.MirrorCS", {"start": v(23, -9.3) * mm, "end": v(23, -8.38) * mm});
            skLineSegment(sketch, "E204.0.MirrorCS", {"start": v(23, -8.38) * mm, "end": v(26.2, -8.38) * mm});
            skLineSegment(sketch, "E205.0.MirrorCS", {"start": v(26.2, -8.38) * mm, "end": v(26.2, -6.81) * mm});
            skLineSegment(sketch, "E206.0.MirrorCS", {"start": v(26.2, -6.81) * mm, "end": v(23.8, -4.41) * mm});
            skLineSegment(sketch, "E207.0.MirrorCS", {"start": v(23.8, -4.41) * mm, "end": v(20.57, -4.41) * mm});
            skLineSegment(sketch, "E208.0.MirrorCS", {"start": v(20.57, -4.41) * mm, "end": v(20, -3.84) * mm});
            skLineSegment(sketch, "E209.0.MirrorCS", {"start": v(20, -3.84) * mm, "end": v(19.42, -4.41) * mm});
            skLineSegment(sketch, "E210.0.MirrorCS", {"start": v(19.42, -4.41) * mm, "end": v(16.2, -4.41) * mm});
            skLineSegment(sketch, "E211.0.MirrorCS", {"start": v(16.2, -4.41) * mm, "end": v(13.8, -6.81) * mm});
            skLineSegment(sketch, "E212.0.MirrorCS", {"start": v(13.8, -6.81) * mm, "end": v(13.8, -8.38) * mm});
            skLineSegment(sketch, "E213.0.MirrorCS", {"start": v(13.8, -8.38) * mm, "end": v(17, -8.38) * mm});
            skLineSegment(sketch, "E214.0.MirrorCS", {"start": v(17, -8.38) * mm, "end": v(17, -9.3) * mm});
            skLineSegment(sketch, "E215.0.MirrorCS", {"start": v(17, -9.3) * mm, "end": v(16.48, -9.3) * mm});
            skLineSegment(sketch, "E216.0.MirrorCS", {"start": v(16.48, -9.3) * mm, "end": v(16.48, -9.91) * mm});
            skLineSegment(sketch, "E217.0.MirrorCS", {"start": v(15.5, -3.71) * mm, "end": v(15.5, -0.4) * mm});
            skLineSegment(sketch, "E218.0.MirrorCS", {"start": v(15.5, -0.4) * mm, "end": v(16, 0.09) * mm});
            skLineSegment(sketch, "E219.0.MirrorCS", {"start": v(16, 0.09) * mm, "end": v(15.5, 0.56) * mm});
            skLineSegment(sketch, "E220.0.MirrorCS", {"start": v(15.5, 0.56) * mm, "end": v(15.5, 3.89) * mm});
            skArc(sketch, "E221.0.MirrorCS", {"start": v(17.44, -0.93) * mm, "mid": v(17.24, 0.09) * mm, "end": v(17.44, 1.1) * mm});
            skLineSegment(sketch, "E222.0.MirrorCS", {"start": v(17.44, 1.1) * mm, "end": v(17, 1.54) * mm});
            skLineSegment(sketch, "E223.0.MirrorCS", {"start": v(17, 1.54) * mm, "end": v(18.54, 3.08) * mm});
            skArc(sketch, "E224.0.MirrorCS", {"start": v(18.98, 2.64) * mm, "mid": v(20, 2.84) * mm, "end": v(21.01, 2.64) * mm});
            skLineSegment(sketch, "E225.0.MirrorCS", {"start": v(21.01, 2.64) * mm, "end": v(21.45, 3.08) * mm});
            skLineSegment(sketch, "E226.0.MirrorCS", {"start": v(21.45, 3.08) * mm, "end": v(22.98, 1.54) * mm});
            skLineSegment(sketch, "E227.0.MirrorCS", {"start": v(22.98, 1.54) * mm, "end": v(22.55, 1.1) * mm});
            skArc(sketch, "E228.0.MirrorCS", {"start": v(22.55, 1.1) * mm, "mid": v(22.74, 0.09) * mm, "end": v(22.55, -0.93) * mm});
            skLineSegment(sketch, "E229.0.MirrorCS", {"start": v(22.55, -0.93) * mm, "end": v(22.98, -1.37) * mm});
            skLineSegment(sketch, "E230.0.MirrorCS", {"start": v(22.98, -1.37) * mm, "end": v(21.45, -2.9) * mm});
            skLineSegment(sketch, "E231.0.MirrorCS", {"start": v(21.45, -2.9) * mm, "end": v(21.01, -2.47) * mm});
            skArc(sketch, "E232.0.MirrorCS", {"start": v(21.01, -2.47) * mm, "mid": v(20, -2.66) * mm, "end": v(18.98, -2.47) * mm});
            skLineSegment(sketch, "E233.0.MirrorCS", {"start": v(18.98, -2.47) * mm, "end": v(18.54, -2.9) * mm});
            skLineSegment(sketch, "E234.0.MirrorCS", {"start": v(18.54, -2.9) * mm, "end": v(17, -1.37) * mm});
            skLineSegment(sketch, "E235.0.MirrorCS", {"start": v(17, -1.37) * mm, "end": v(17.44, -0.93) * mm});
            skLineSegment(sketch, "E236.0.MirrorCS", {"start": v(18.54, 3.08) * mm, "end": v(18.98, 2.64) * mm});
            skLineSegment(sketch, "E237", {"start": v(3.51, 10.09) * mm, "end": v(16.48, 10.09) * mm});
            skLineSegment(sketch, "E238", {"start": v(3.51, -9.91) * mm, "end": v(16.48, -9.91) * mm});
            skLineSegment(sketch, "E239", {"start": v(0.8, 8.55) * mm, "end": v(20.5, 8.55) * mm, "construction": true});
            skLineSegment(sketch, "E240", {"start": v(0.52, -8.38) * mm, "end": v(20.42, -8.38) * mm, "construction": true});
            skLineSegment(sketch, "E241", {"start": v(4.5, -3.71) * mm, "end": v(12.34, -11.56) * mm, "construction": true});
            skLineSegment(sketch, "E242", {"start": v(15.5, -3.71) * mm, "end": v(7.46, -11.75) * mm, "construction": true});
            skLineSegment(sketch, "E243", {"start": v(4.5, 3.89) * mm, "end": v(12.58, 11.95) * mm, "construction": true});
            skLineSegment(sketch, "E244", {"start": v(15.5, 3.89) * mm, "end": v(7.44, 11.96) * mm, "construction": true});
            skLineSegment(sketch, "E245", {"start": v(7.18, 8.55) * mm, "end": v(7.18, 6.57) * mm});
            skLineSegment(sketch, "E246.0.MirrorCS", {"start": v(12.8, 8.55) * mm, "end": v(12.8, 6.57) * mm});
            skLineSegment(sketch, "E247", {"start": v(4.5, 3.89) * mm, "end": v(7.18, 6.57) * mm});
            skLineSegment(sketch, "E248", {"start": v(7.18, 8.55) * mm, "end": v(12.8, 8.55) * mm});
            skLineSegment(sketch, "E249", {"start": v(12.8, 6.57) * mm, "end": v(15.5, 3.89) * mm});
            skLineSegment(sketch, "E250", {"start": v(7.18, -8.38) * mm, "end": v(7.18, -6.4) * mm});
            skLineSegment(sketch, "E251", {"start": v(7.18, -6.4) * mm, "end": v(4.5, -3.71) * mm});
            skLineSegment(sketch, "E252", {"start": v(12.8, -8.38) * mm, "end": v(12.8, -6.4) * mm});
            skLineSegment(sketch, "E253", {"start": v(12.8, -6.4) * mm, "end": v(15.5, -3.71) * mm});
            skLineSegment(sketch, "E254", {"start": v(7.18, -8.38) * mm, "end": v(12.8, -8.38) * mm});
            skSolve(sketch);
        }
        {
            var Q0;
            Q0=qSketchRegion(id+"F0",true);
            extrude(context, id + "F2", {"entities" : qUnion([Q0]), "depth" : 100 * mm});
        }
        {
            var Q0;
            Q0=qSketchRegion(id+"F1",true);
            extrude(context, id + "F3", {"entities" : qUnion([Q0]), "depth" : 80 * mm});
        }
        {
            var Q0;
            Q0 = qSketchRegion(id + "F1", true);
            extrude(context, id + "F4", {"entities" : qUnion([Q0]), "oppositeDirection" : true, "depth" : 540 * mm});
        }
        {
            var Q0;
            Q0 = qSketchRegion(id + "F1", true);
            extrude(context, id + "F5", {"entities" : qUnion([Q0]), "oppositeDirection" : true, "depth" : 500 * mm});
        }
        {
            var Q0;
            Q0 = qSketchRegion(id + "F0", true);
            extrude(context, id + "F6", {"entities" : qUnion([Q0]), "depth" : 55 * mm});
        }
        {
            var Q0;
            Q0 = qSketchRegion(id + "F1", true);
            extrude(context, id + "F7", {"entities" : qUnion([Q0]), "depth" : 55 * mm});
        }
        {
            var Q0;
            Q0 = qSketchRegion(id + "F0", true);
            extrude(context, id + "F8", {"entities" : qUnion([Q0]), "depth" : 540 * mm});
        }
        {
            var Q0;
            Q0 = qSketchRegion(id + "F0", true);
            extrude(context, id + "F9", {"entities" : qUnion([Q0]), "depth" : 650 * mm});
        }
        {
            var Q0;
            Q0 = qSketchRegion(id + "F0", true);
            extrude(context, id + "F10", {"entities" : qUnion([Q0]), "depth" : 500 * mm});
        }
    });
